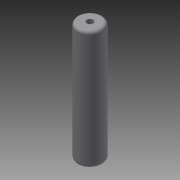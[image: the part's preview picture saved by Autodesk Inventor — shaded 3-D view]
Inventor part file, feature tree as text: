
AUTODESK INVENTOR PART (.ipt)
format: ipt  version: 2014 (Build 180170000, 170)  size: 87,040 bytes
history: native  units: mm
features: extrude x1, fillet x1, sketch x1
ambient origin geometry x8: Origin, YZ Plane, XZ Plane, XY Plane, X Axis, Y Axis, Z Axis, Center Point
bodies: Solid1 (feature_tree)
feature tree (3):
  extrude  "Extrusion1"  Depth=3.0mm
  fillet  "Fillet1"  Radius=120.65mm
  sketch  "Sketch1"  dims[d0=25.4mm d1=6.604mm d2=120.65mm d3=0.0mm d4=3.0mm]
